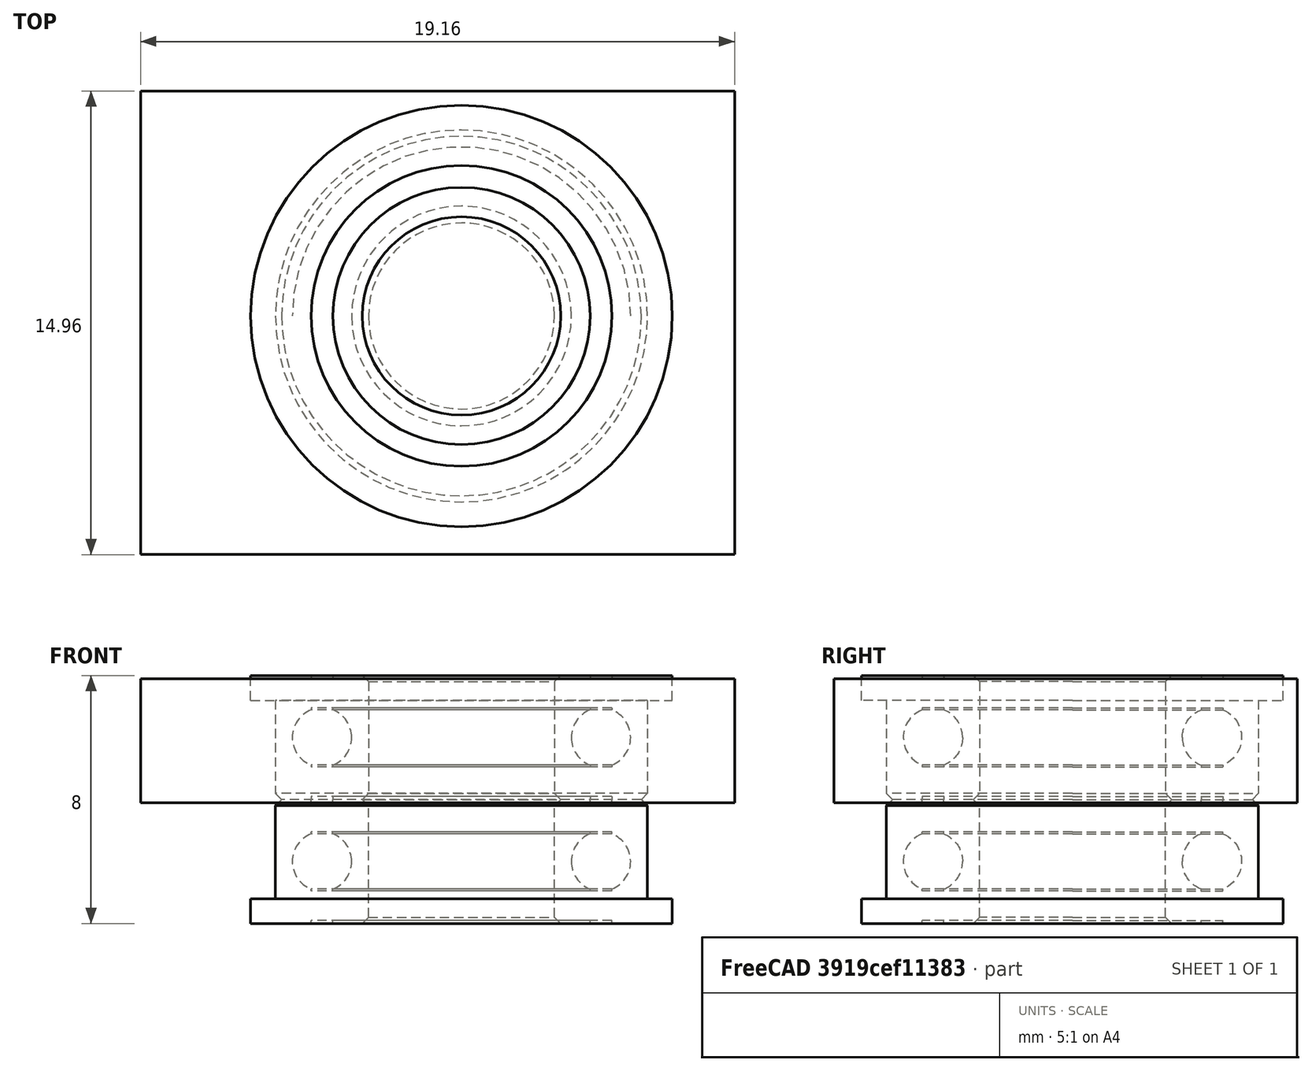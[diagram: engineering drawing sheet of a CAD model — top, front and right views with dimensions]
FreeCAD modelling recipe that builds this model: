
FCSTD DOCUMENT  (FreeCAD 0.16R6707 (Git))
Label: D3D Idler Pulley
License: CreativeCommons Attribution
LicenseURL: http://creativecommons.org/licenses/by/4.0/
objects: Part::Feature×1, Sketcher::SketchObject×1, PartDesign::Pocket×1
note: 4 computed .brp shape members not serialized (recipe doc carries the construction recipe); baked Part::Feature solids carry a one-line shape summary decoded from their .brp

FEATURE [Part::Feature] Part__Feature  label="ball_bearing"
  shape: bbox 13.6 x 13.6 x 8 mm, 82 faces (baked)
FEATURE [Sketcher::SketchObject] Sketch
  Placement = pos=(0,0,5.9) rot=(0,0,1;0rad)
  Support = -> Part__Feature [Face33]
  sketch-geometry (4):
    g0: LineSegment StartX=-10.3538 StartY=7.25931 StartZ=0 EndX=8.80934 EndY=7.25931 EndZ=0
    g1: LineSegment StartX=8.80934 StartY=7.25931 StartZ=0 EndX=8.80934 EndY=-7.69594 EndZ=0
    g2: LineSegment StartX=8.80934 StartY=-7.69594 StartZ=0 EndX=-10.3538 EndY=-7.69594 EndZ=0
    g3: LineSegment StartX=-10.3538 StartY=-7.69594 StartZ=0 EndX=-10.3538 EndY=7.25931 EndZ=0
  constraints (8):
    c: Coincident(g0,g1)
    c: Coincident(g1,g2)
    c: Coincident(g2,g3)
    c: Coincident(g3,g0)
    c: Horizontal(g0)
    c: Horizontal(g2)
    c: Vertical(g1)
    c: Vertical(g3)
FEATURE [PartDesign::Pocket] Pocket
  Length = 3.99999
  Sketch = -> Sketch
  Type = 0
